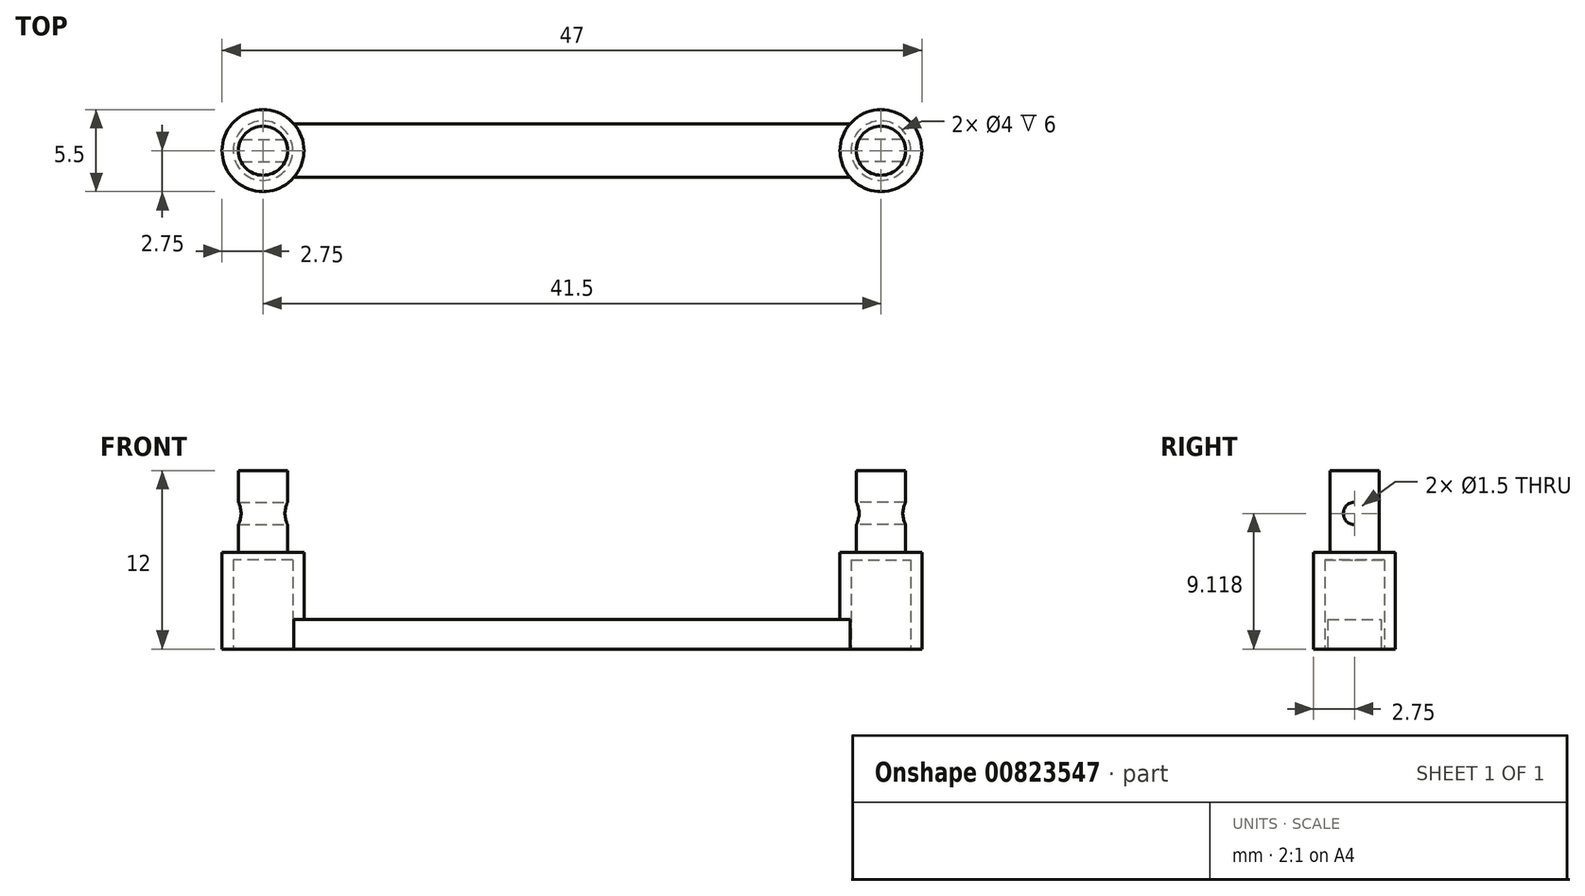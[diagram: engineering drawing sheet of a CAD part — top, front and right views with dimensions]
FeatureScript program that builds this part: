
annotation { "Feature Type Name" : "Feature", "Feature Type Description" : "" }
export const myFeature = defineFeature(function(context is Context, id is Id, definition is map)
    precondition{}
    {
        {
            var Q0;
            Q0=qCreatedBy(makeId("Top.planeOp"),FACE);
            var sketch = newSketch(context, id + "F0", { "sketchPlane" : qUnion([Q0])});
            skLineSegment(sketch, "E0", {"start": v(0, 0) * mm, "end": v(-20.75, 0) * mm});
            skCircle(sketch, "E1", {"center": v(-20.75, 0) * mm, "radius": 2 * mm});
            skCircle(sketch, "E2", {"center": v(-20.75, 0) * mm, "radius": 2.75 * mm});
            skLineSegment(sketch, "E3", {"start": v(0, 0) * mm, "end": v(0, 1.8) * mm});
            skLineSegment(sketch, "E4", {"start": v(0, 0) * mm, "end": v(0, -1.8) * mm});
            skLineSegment(sketch, "E5", {"start": v(0, -1.8) * mm, "end": v(-18.67, -1.8) * mm});
            skLineSegment(sketch, "E6", {"start": v(0, 1.8) * mm, "end": v(-18.67, 1.8) * mm});
            skLineSegment(sketch, "E7", {"start": v(-20.75, 0) * mm, "end": v(-20.75, 4) * mm});
            skLineSegment(sketch, "E8", {"start": v(-20.75, 4) * mm, "end": v(-19, 4) * mm});
            skLineSegment(sketch, "E9", {"start": v(-20.75, 4) * mm, "end": v(-22.5, 4) * mm});
            skLineSegment(sketch, "E10", {"start": v(-19, 4) * mm, "end": v(-19, 2.12) * mm});
            skLineSegment(sketch, "E11", {"start": v(-22.5, 4) * mm, "end": v(-22.5, 2.12) * mm});
            skSolve(sketch);
        }
        {
            var Q0;
            Q0=makeQuery(id+"F0.imprint","IMPRINT",FACE,{"disambiguationData":[TD([[makeQuery(id+"F0.imprint","IMPRINT",EDGE,{"derivedFrom":sQuery(id+"F0.wireOp",EDGE,"E1")}),-1.0]])]});
            extrude(context, id + "F1", {"entities" : qUnion([Q0]), "depth" : 6 * mm, "offsetDistance" : 25 * mm});
        }
        {
            var Q0;
            {var subQ0=sQuery(id+"F0.wireOp",EDGE,"E3");Q0=makeQuery(id+"F0.imprint","IMPRINT",FACE,{"disambiguationData":[TD([[makeQuery(id+"F0.imprint","IMPRINT",EDGE,{"derivedFrom":subQ0}),1.0]])]});}
            var Q1;
            {var subQ0=sQuery(id+"F0.wireOp",EDGE,"E4");Q1=makeQuery(id+"F0.imprint","IMPRINT",FACE,{"disambiguationData":[TD([[makeQuery(id+"F0.imprint","IMPRINT",EDGE,{"derivedFrom":subQ0}),-1.0]])]});}
            extrude(context, id + "F2", {"entities" : qUnion([Q0, Q1]), "operationType" : NewBodyOperationType.ADD, "depth" : 2 * mm, "offsetDistance" : 25 * mm});
        }
        {
            var Q0;
            Q0=makeQuery(id+"F1.opExtrude","CAP_FACE",FACE,{"disambiguationData":[OSD([sQuery(id+"F0.wireOp",EDGE,"E1"),sQuery(id+"F0.wireOp",EDGE,"E2")])],"isStart":false});
            var sketch = newSketch(context, id + "F3", { "sketchPlane" : qUnion([Q0])});
            skCircle(sketch, "E12", {"center": v(-20.75, 0) * mm, "radius": 2.75 * mm});
            skSolve(sketch);
        }
        {
            var Q0;
            Q0=makeQuery(id+"F3.imprint","IMPRINT",FACE,{"disambiguationData":[TD([[makeQuery(id+"F3.imprint","IMPRINT",EDGE,{"derivedFrom":makeQuery(id+"F1.opExtrude","CAP_EDGE",EDGE,{"disambiguationData":[OSD([sQuery(id+"F0.wireOp",EDGE,"E1")])],"isStart":false})}),1.0]])]});
            var Q1;
            Q1=makeQuery(id+"F3.imprint","IMPRINT",FACE,{"disambiguationData":[TD([[makeQuery(id+"F3.imprint","IMPRINT",EDGE,{"derivedFrom":sQuery(id+"F3.wireOp",EDGE,"E12")}),1.0]])]});
            extrude(context, id + "F4", {"entities" : qUnion([Q0, Q1]), "operationType" : NewBodyOperationType.ADD, "depth" : .5 * mm, "offsetDistance" : 25 * mm});
        }
        {
            var Q0;
            Q0=makeQuery(id+"F4.opExtrude","CAP_FACE",FACE,{"disambiguationData":[OSD([sQuery(id+"F3.wireOp",EDGE,"E12")])],"isStart":false});
            var sketch = newSketch(context, id + "F5", { "sketchPlane" : qUnion([Q0])});
            skCircle(sketch, "E13", {"center": v(-20.75, 0) * mm, "radius": 1.65 * mm});
            skSolve(sketch);
        }
        {
            var Q0;
            Q0=makeQuery(id+"F5.imprint","IMPRINT",FACE,{"disambiguationData":[TD([[makeQuery(id+"F5.imprint","IMPRINT",EDGE,{"derivedFrom":sQuery(id+"F5.wireOp",EDGE,"E13")}),1.0]])]});
            extrude(context, id + "F6", {"entities" : qUnion([Q0]), "operationType" : NewBodyOperationType.ADD, "depth" : 5.5 * mm, "offsetDistance" : 25 * mm});
        }
        {
            var Q0;
            Q0=qCreatedBy(makeId("Right.planeOp"),FACE);
            cPlane(context, id + "F7", {"entities" : qUnion([Q0]), "cplaneType" : CPlaneType.OFFSET, "offset" : 1 * mm, "width" : 150 * mm, "height" : 150 * mm});
        }
        {
            var Q0;
            Q0=qCreatedBy(id+"F7.planeOp",FACE);
            var sketch = newSketch(context, id + "F8", { "sketchPlane" : qUnion([Q0])});
            skCircle(sketch, "E14", {"center": v(0, 9.12) * mm, "radius": 0.75 * mm});
            skSolve(sketch);
        }
        {
            var Q0;
            Q0=makeQuery(id+"F8.imprint","IMPRINT",FACE,{"disambiguationData":[TD([[makeQuery(id+"F8.imprint","IMPRINT",EDGE,{"derivedFrom":sQuery(id+"F8.wireOp",EDGE,"E14")}),1.0]])]});
            extrude(context, id + "F9", {"entities" : qUnion([Q0]), "operationType" : NewBodyOperationType.REMOVE, "endBound" : BoundingType.THROUGH_ALL, "oppositeDirection" : true, "depth" : 5 * mm, "offsetDistance" : 25 * mm});
        }
        {
            var Q0;
            Q0=makeQuery(id+"F1.opExtrude","SWEPT_BODY",BODY,{"disambiguationData":[OSD([sQuery(id+"F0.wireOp",EDGE,"E1"),sQuery(id+"F0.wireOp",EDGE,"E2")])]});
            var Q1;
            Q1=qCreatedBy(makeId("Right.planeOp"),FACE);
            mirror(context, id + "F10", {"operationType" : NewBodyOperationType.ADD, "entities" : qUnion([Q0]), "mirrorPlane" : qUnion([Q1])});
        }
    });
